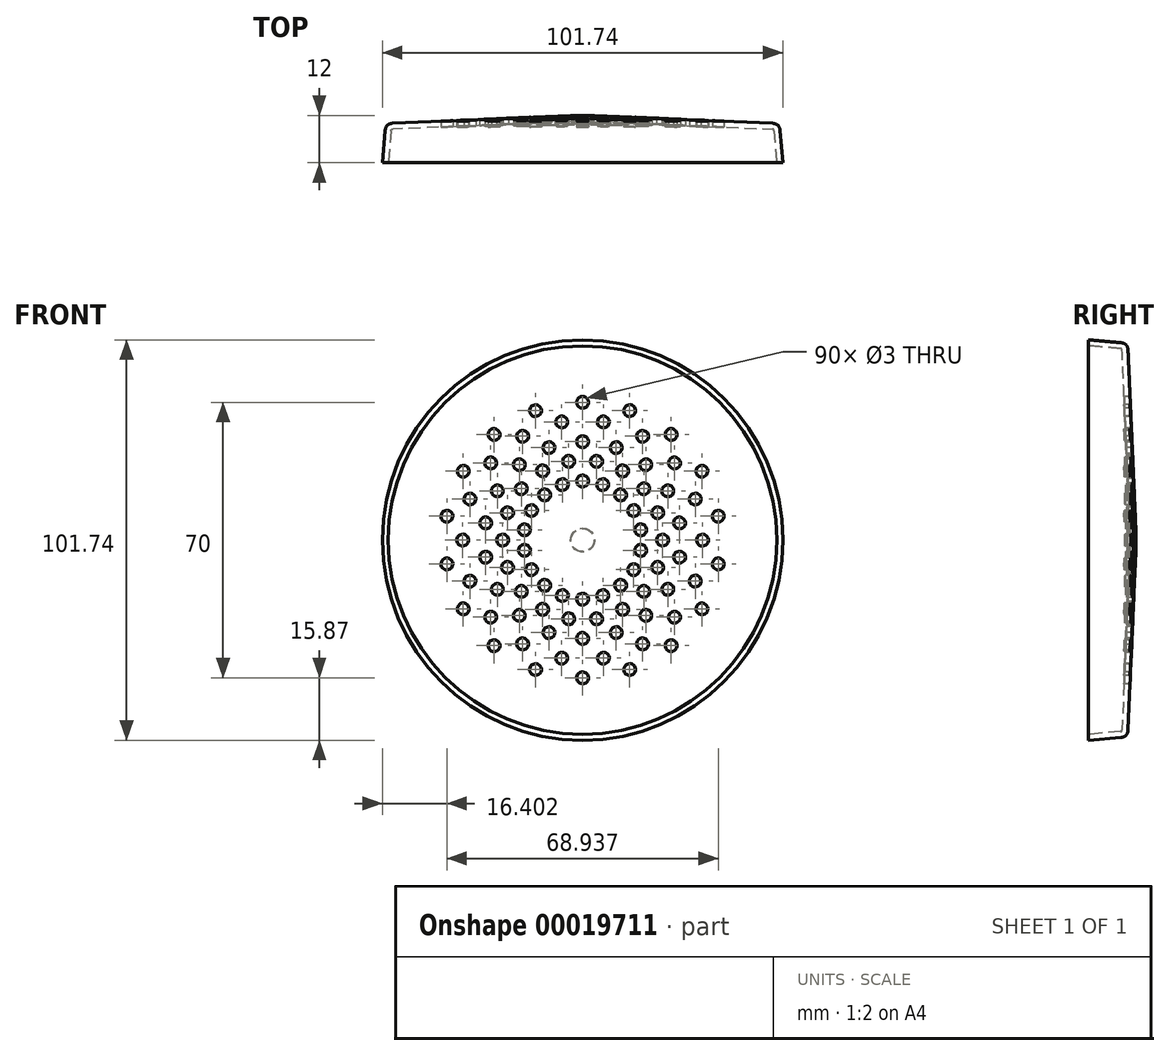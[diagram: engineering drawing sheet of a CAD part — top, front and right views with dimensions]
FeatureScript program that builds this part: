
annotation { "Feature Type Name" : "Feature", "Feature Type Description" : "" }
export const myFeature = defineFeature(function(context is Context, id is Id, definition is map)
    precondition{}
    {
        {
            var Q0;
            Q0=qCreatedBy(makeId("Top.planeOp"),FACE);
            var sketch = newSketch(context, id + "F0", { "sketchPlane" : qUnion([Q0])});
            skLineSegment(sketch, "E0", {"start": v(50, 9.95) * mm, "end": v(50.87, 0) * mm});
            skLineSegment(sketch, "E1", {"start": v(0, 0) * mm, "end": v(50.87, 0) * mm});
            skLineSegment(sketch, "E2", {"start": v(0, 12) * mm, "end": v(0, 0) * mm});
            skLineSegment(sketch, "E3", {"start": v(0, 16.8) * mm, "end": v(0, -6.24) * mm, "construction": true});
            skLineSegment(sketch, "E4", {"start": v(0, 12) * mm, "end": v(3, 12) * mm});
            skLineSegment(sketch, "E5", {"start": v(3, 12) * mm, "end": v(50, 9.95) * mm});
            skSolve(sketch);
        }
        {
            var Q0;
            Q0 = qSketchRegion(id + "F0", true);
            var Q1;
            Q1=sQuery(id+"F0.wireOp",EDGE,"E3");
            revolve(context, id + "F1", {"entities" : qUnion([Q0]), "axis" : qUnion([Q1]), "revolveType" : RevolveType.FULL});
        }
        {
            var Q0;
            Q0=makeQuery(id+"F1.opRevolve","SWEPT_EDGE",EDGE,{"disambiguationData":[OSD([sQuery(id+"F0.wireOp",EDGE,"E0"),sQuery(id+"F0.wireOp",EDGE,"E5")])]});
            fillet(context, id + "F2", {"entities" : qUnion([Q0]), "radius" : 2 * mm, "tangentPropagation" : true, "rho" : 0.5, "crossSection" : FilletCrossSection.CONIC, "allowEdgeOverflow" : false});
        }
        {
            var Q0;
            Q0=makeQuery(id+"F1.opRevolve","SWEPT_EDGE",EDGE,{"disambiguationData":[OSD([sQuery(id+"F0.wireOp",EDGE,"E4"),sQuery(id+"F0.wireOp",EDGE,"E5")])]});
            fillet(context, id + "F3", {"entities" : qUnion([Q0]), "radius" : 2 * mm, "tangentPropagation" : true, "rho" : 0.5, "crossSection" : FilletCrossSection.CONIC, "allowEdgeOverflow" : false});
        }
        {
            var Q0;
            Q0=makeQuery(id+"F1.opRevolve","SWEPT_FACE",FACE,{"disambiguationData":[OSD([sQuery(id+"F0.wireOp",EDGE,"E1")])]});
            shell(context, id + "F4", {"entities" : qUnion([Q0]), "thickness" : 1.5 * mm});
        }
        {
            var Q0;
            Q0=qCreatedBy(makeId("Front.planeOp"),FACE);
            var sketch = newSketch(context, id + "F5", { "sketchPlane" : qUnion([Q0])});
            skLineSegment(sketch, "E6", {"start": v(0, 0) * mm, "end": v(0, 35) * mm, "construction": true});
            skLineSegment(sketch, "E7", {"start": v(0, 0) * mm, "end": v(5.29, 30) * mm, "construction": true});
            skPoint(sketch, "E8", {"position": v(0, 25) * mm});
            skPoint(sketch, "E9", {"position": v(3.53, 20) * mm});
            skPoint(sketch, "E10", {"position": v(0, 15) * mm});
            skCircle(sketch, "E11", {"center": v(0, 35) * mm, "radius": 1.5 * mm});
            skCircle(sketch, "E12", {"center": v(5.29, 30) * mm, "radius": 1.5 * mm});
            skCircle(sketch, "E13", {"center": v(0, 25) * mm, "radius": 1.5 * mm});
            skCircle(sketch, "E14", {"center": v(3.53, 20) * mm, "radius": 1.5 * mm});
            skCircle(sketch, "E15", {"center": v(0, 15) * mm, "radius": 1.5 * mm});
            skCircle(sketch, "E16.1.0", {"center": v(-5.29, 30) * mm, "radius": 1.5 * mm});
            skCircle(sketch, "E16.1.1", {"center": v(-11.97, 32.89) * mm, "radius": 1.5 * mm});
            skCircle(sketch, "E16.1.2", {"center": v(-8.55, 23.5) * mm, "radius": 1.5 * mm});
            skCircle(sketch, "E16.1.3", {"center": v(-3.53, 20) * mm, "radius": 1.5 * mm});
            skCircle(sketch, "E16.1.4", {"center": v(-5.13, 14.1) * mm, "radius": 1.5 * mm});
            skCircle(sketch, "E16.2.0", {"center": v(-15.23, 26.38) * mm, "radius": 1.5 * mm});
            skCircle(sketch, "E16.2.1", {"center": v(-22.5, 26.81) * mm, "radius": 1.5 * mm});
            skCircle(sketch, "E16.2.2", {"center": v(-16.07, 19.15) * mm, "radius": 1.5 * mm});
            skCircle(sketch, "E16.2.3", {"center": v(-10.15, 17.59) * mm, "radius": 1.5 * mm});
            skCircle(sketch, "E16.2.4", {"center": v(-9.64, 11.5) * mm, "radius": 1.5 * mm});
            skCircle(sketch, "E16.3.0", {"center": v(-23.34, 19.58) * mm, "radius": 1.5 * mm});
            skCircle(sketch, "E16.3.1", {"center": v(-30.31, 17.5) * mm, "radius": 1.5 * mm});
            skCircle(sketch, "E16.3.2", {"center": v(-21.65, 12.5) * mm, "radius": 1.5 * mm});
            skCircle(sketch, "E16.3.3", {"center": v(-15.56, 13.05) * mm, "radius": 1.5 * mm});
            skCircle(sketch, "E16.3.4", {"center": v(-13, 7.5) * mm, "radius": 1.5 * mm});
            skCircle(sketch, "E16.4.0", {"center": v(-28.63, 10.42) * mm, "radius": 1.5 * mm});
            skCircle(sketch, "E16.4.1", {"center": v(-34.47, 6.08) * mm, "radius": 1.5 * mm});
            skCircle(sketch, "E16.4.2", {"center": v(-24.62, 4.34) * mm, "radius": 1.5 * mm});
            skCircle(sketch, "E16.4.3", {"center": v(-19.08, 6.95) * mm, "radius": 1.5 * mm});
            skCircle(sketch, "E16.4.4", {"center": v(-14.77, 2.6) * mm, "radius": 1.5 * mm});
            skCircle(sketch, "E16.5.0", {"center": v(-30.46, 0) * mm, "radius": 1.5 * mm});
            skCircle(sketch, "E16.5.1", {"center": v(-34.47, -6.08) * mm, "radius": 1.5 * mm});
            skCircle(sketch, "E16.5.2", {"center": v(-24.62, -4.34) * mm, "radius": 1.5 * mm});
            skCircle(sketch, "E16.5.3", {"center": v(-20.3, 0) * mm, "radius": 1.5 * mm});
            skCircle(sketch, "E16.5.4", {"center": v(-14.77, -2.6) * mm, "radius": 1.5 * mm});
            skCircle(sketch, "E16.6.0", {"center": v(-28.63, -10.42) * mm, "radius": 1.5 * mm});
            skCircle(sketch, "E16.6.1", {"center": v(-30.31, -17.5) * mm, "radius": 1.5 * mm});
            skCircle(sketch, "E16.6.2", {"center": v(-21.65, -12.5) * mm, "radius": 1.5 * mm});
            skCircle(sketch, "E16.6.3", {"center": v(-19.08, -6.95) * mm, "radius": 1.5 * mm});
            skCircle(sketch, "E16.6.4", {"center": v(-13, -7.5) * mm, "radius": 1.5 * mm});
            skCircle(sketch, "E16.7.0", {"center": v(-23.34, -19.58) * mm, "radius": 1.5 * mm});
            skCircle(sketch, "E16.7.1", {"center": v(-22.5, -26.81) * mm, "radius": 1.5 * mm});
            skCircle(sketch, "E16.7.2", {"center": v(-16.07, -19.15) * mm, "radius": 1.5 * mm});
            skCircle(sketch, "E16.7.3", {"center": v(-15.56, -13.05) * mm, "radius": 1.5 * mm});
            skCircle(sketch, "E16.7.4", {"center": v(-9.64, -11.5) * mm, "radius": 1.5 * mm});
            skCircle(sketch, "E16.8.0", {"center": v(-15.23, -26.38) * mm, "radius": 1.5 * mm});
            skCircle(sketch, "E16.8.1", {"center": v(-11.97, -32.89) * mm, "radius": 1.5 * mm});
            skCircle(sketch, "E16.8.2", {"center": v(-8.55, -23.5) * mm, "radius": 1.5 * mm});
            skCircle(sketch, "E16.8.3", {"center": v(-10.15, -17.59) * mm, "radius": 1.5 * mm});
            skCircle(sketch, "E16.8.4", {"center": v(-5.13, -14.1) * mm, "radius": 1.5 * mm});
            skCircle(sketch, "E16.9.0", {"center": v(-5.29, -30) * mm, "radius": 1.5 * mm});
            skCircle(sketch, "E16.9.1", {"center": v(0, -35) * mm, "radius": 1.5 * mm});
            skCircle(sketch, "E16.9.2", {"center": v(0, -25) * mm, "radius": 1.5 * mm});
            skCircle(sketch, "E16.9.3", {"center": v(-3.53, -20) * mm, "radius": 1.5 * mm});
            skCircle(sketch, "E16.9.4", {"center": v(0, -15) * mm, "radius": 1.5 * mm});
            skCircle(sketch, "E16.10.0", {"center": v(5.29, -30) * mm, "radius": 1.5 * mm});
            skCircle(sketch, "E16.10.1", {"center": v(11.97, -32.89) * mm, "radius": 1.5 * mm});
            skCircle(sketch, "E16.10.2", {"center": v(8.55, -23.5) * mm, "radius": 1.5 * mm});
            skCircle(sketch, "E16.10.3", {"center": v(3.53, -20) * mm, "radius": 1.5 * mm});
            skCircle(sketch, "E16.10.4", {"center": v(5.13, -14.1) * mm, "radius": 1.5 * mm});
            skCircle(sketch, "E16.11.0", {"center": v(15.23, -26.38) * mm, "radius": 1.5 * mm});
            skCircle(sketch, "E16.11.1", {"center": v(22.5, -26.81) * mm, "radius": 1.5 * mm});
            skCircle(sketch, "E16.11.2", {"center": v(16.07, -19.15) * mm, "radius": 1.5 * mm});
            skCircle(sketch, "E16.11.3", {"center": v(10.15, -17.59) * mm, "radius": 1.5 * mm});
            skCircle(sketch, "E16.11.4", {"center": v(9.64, -11.5) * mm, "radius": 1.5 * mm});
            skCircle(sketch, "E16.12.0", {"center": v(23.34, -19.58) * mm, "radius": 1.5 * mm});
            skCircle(sketch, "E16.12.1", {"center": v(30.31, -17.5) * mm, "radius": 1.5 * mm});
            skCircle(sketch, "E16.12.2", {"center": v(21.65, -12.5) * mm, "radius": 1.5 * mm});
            skCircle(sketch, "E16.12.3", {"center": v(15.56, -13.05) * mm, "radius": 1.5 * mm});
            skCircle(sketch, "E16.12.4", {"center": v(13, -7.5) * mm, "radius": 1.5 * mm});
            skCircle(sketch, "E16.13.0", {"center": v(28.63, -10.42) * mm, "radius": 1.5 * mm});
            skCircle(sketch, "E16.13.1", {"center": v(34.47, -6.08) * mm, "radius": 1.5 * mm});
            skCircle(sketch, "E16.13.2", {"center": v(24.62, -4.34) * mm, "radius": 1.5 * mm});
            skCircle(sketch, "E16.13.3", {"center": v(19.08, -6.95) * mm, "radius": 1.5 * mm});
            skCircle(sketch, "E16.13.4", {"center": v(14.77, -2.6) * mm, "radius": 1.5 * mm});
            skCircle(sketch, "E16.14.0", {"center": v(30.46, 0) * mm, "radius": 1.5 * mm});
            skCircle(sketch, "E16.14.1", {"center": v(34.47, 6.08) * mm, "radius": 1.5 * mm});
            skCircle(sketch, "E16.14.2", {"center": v(24.62, 4.34) * mm, "radius": 1.5 * mm});
            skCircle(sketch, "E16.14.3", {"center": v(20.3, 0) * mm, "radius": 1.5 * mm});
            skCircle(sketch, "E16.14.4", {"center": v(14.77, 2.6) * mm, "radius": 1.5 * mm});
            skCircle(sketch, "E16.15.0", {"center": v(28.63, 10.42) * mm, "radius": 1.5 * mm});
            skCircle(sketch, "E16.15.1", {"center": v(30.31, 17.5) * mm, "radius": 1.5 * mm});
            skCircle(sketch, "E16.15.2", {"center": v(21.65, 12.5) * mm, "radius": 1.5 * mm});
            skCircle(sketch, "E16.15.3", {"center": v(19.08, 6.95) * mm, "radius": 1.5 * mm});
            skCircle(sketch, "E16.15.4", {"center": v(13, 7.5) * mm, "radius": 1.5 * mm});
            skCircle(sketch, "E16.16.0", {"center": v(23.34, 19.58) * mm, "radius": 1.5 * mm});
            skCircle(sketch, "E16.16.1", {"center": v(22.5, 26.81) * mm, "radius": 1.5 * mm});
            skCircle(sketch, "E16.16.2", {"center": v(16.07, 19.15) * mm, "radius": 1.5 * mm});
            skCircle(sketch, "E16.16.3", {"center": v(15.56, 13.05) * mm, "radius": 1.5 * mm});
            skCircle(sketch, "E16.16.4", {"center": v(9.64, 11.5) * mm, "radius": 1.5 * mm});
            skCircle(sketch, "E16.17.0", {"center": v(15.23, 26.38) * mm, "radius": 1.5 * mm});
            skCircle(sketch, "E16.17.1", {"center": v(11.97, 32.89) * mm, "radius": 1.5 * mm});
            skCircle(sketch, "E16.17.2", {"center": v(8.55, 23.5) * mm, "radius": 1.5 * mm});
            skCircle(sketch, "E16.17.3", {"center": v(10.15, 17.59) * mm, "radius": 1.5 * mm});
            skCircle(sketch, "E16.17.4", {"center": v(5.13, 14.1) * mm, "radius": 1.5 * mm});
            skPoint(sketch, "E16.center", {"position": v(0, 0) * mm});
            skSolve(sketch);
        }
        {
            var Q0;
            Q0 = qSketchRegion(id + "F5", true);
            extrude(context, id + "F6", {"entities" : qUnion([Q0]), "operationType" : NewBodyOperationType.REMOVE, "endBound" : BoundingType.THROUGH_ALL, "oppositeDirection" : true, "depth" : 25 * mm});
        }
    });
